# Revit family: Heavy_Duty_Bi-Level Fountain_integral_soft_sides-elkay-EHWM17C
name_source: partatom
category: Plumbing Fixtures
units: mm (PartAtom-declared; Revit-internal decimal feet)

## family parameters
Cut with Voids When Loaded = No
Host = Face
Maintain Annotation Orientation = No
OmniClass Number = 23.65.70.14.11
OmniClass Title = Drinking Fountains/Coolers
Part Type = Normal
Room Calculation Point = No
Round Connector Dimension = Use Diameter
Shared = No

## types (1)
- EHWM17C (Slimline Soft Sides® Heavy Duty Bi-Level Fountain)
    Activation Method = Mechanical Front Bubbler Button
    Approx. Shipping Weight (lbs) = 60
    Assembly Code = D2010
    CW Connection = No
    Chilling Capacity = Non-refrigerated
    Current = 0 A
    Cut Height = 20.38 "
    Default Elevation = 48 "
    Description = Slimline Soft Sides® Heavy Duty Bi-Level Fountain Non-Filtered Non-Refrigerated Stainless
    Dimensions (L x W x H) = 38 1/2 inch x 19 3/8" inch x 20 3/8 inch
    HW Connection = No
    Inlet connection = 0.38 "
    Installation Location = Indoor + Outdoor
    Length = 38.5 "
    Main Material = Finish-Elkay-Stainless Steel
    Manufacturer = Elkay Manufacturer Company
    Manufacturer Brand = Elkay (by Zurn Elkay Water Solutions)
    Model = EHWM17C
    Mounting Type = Wall Mount (On Wall)
    Number of Poles = 1
    Outlet connection = 1.5 "
    Power Factor = 0
    Product Documentation Link = https://www.elkayfiles.com
    Product Installation Sheet URL = https://www.elkayfiles.com
    Product Page URL = https://www.elkay.com
    Product Weight (lbs) = 51
    Product data URL = https://www.bimobject.com
    Repair Parts URL = https://www.elkayfiles.com
    Second material = Elkay-Transparent
    Supply Line = 20.5 "
    URL = https://www.elkay.com
    Vent Connection = No
    Voltage = 115 V
    Waste Connection = No
    Waste Line = 15.5 "
    Width = 34.63 "
    Width of Cut = 38.5 "
    basin radius = 3.9 "
    thickness = 0.63 "

## geometry (parser evidence)
native form markers: Sweep x16
no freeform markers — native parametric forms only
